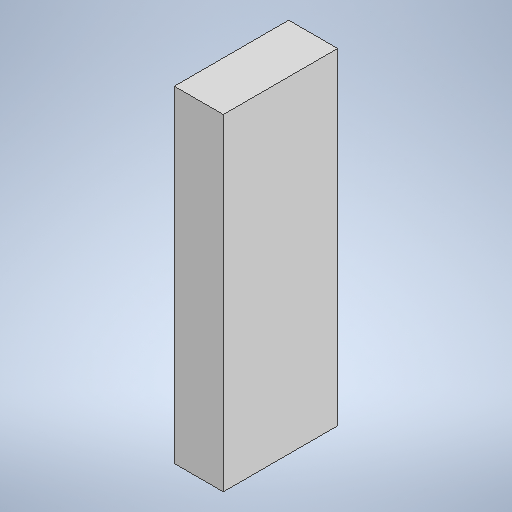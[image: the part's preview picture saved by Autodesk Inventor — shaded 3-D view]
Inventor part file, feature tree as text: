
AUTODESK INVENTOR PART (.ipt)
format: ipt  version: 2025 (Build 290162000, 162)  size: 219,648 bytes
history: native  units: in
note: dims shown in document units (in); Inventor stores cm internally (conversion verified against a paired STEP export)
features: extrude x1, sketch x1
ambient origin geometry x8: Origin, YZ Plane, XZ Plane, XY Plane, X Axis, Y Axis, Z Axis, Center Point
bodies: Solid1 (feature_tree)
feature tree (2):
  extrude  "Extrusion1"  Depth=3.5in
  sketch  "Sketch1"  dims[d0=10.0in d1=3.5in d2=1.5in d3=0.0in]
